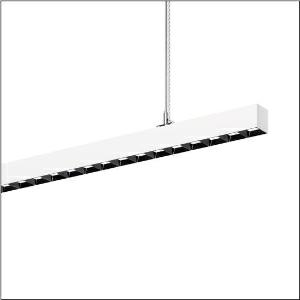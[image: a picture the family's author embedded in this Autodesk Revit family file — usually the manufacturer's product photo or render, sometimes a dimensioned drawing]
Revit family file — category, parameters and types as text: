
# Revit family: silica_r__21_51mx31tctdw_2edc
name_source: partatom
category: Lighting Fixtures
units: mm (PartAtom-declared; Revit-internal decimal feet)

## family parameters
Cut with Voids When Loaded = No
Host = Face
Light Source = No
Part Type = Normal
Room Calculation Point = No
Round Connector Dimension = Use Diameter
Shared = No

## types (1)
- --- (1 x LED, 15550 lm, 133.9 W, 6500K)
    Apparent Load = 134 VA
    CIE Flux Codes = 85 99 100 60 100
    Color Rendering = 80
    Color Temperature = 6500K
    Default Elevation = 1800 mm
    Description = Silica® 21, office luminaire, primary light control with darklight reflector, of PMMA, black, CAT 2 (L<= 3000cd/m²), light emission: direct/indirect distribution, primary light characteristic: symmetric, installation type: suspended mounting, LED, rated luminous flux: 15.550lm, luminous efficacy: 111lm/W, light colour: 8tw, colour temperature: 2700..6500K, control gear: ECG DALI, with terminal, 3+2-pole, max. 2.5mm², mains connection: 220..240V, AC, 50/60Hz, rated input power: 140.6W, luminaire housing, of aluminium, traffic white (RAL 9016), length: 3.004mm, width: 53mm, height: 53mm, protection rating (complete): IP20, insulation class (complete): insulation class I (protective earthing), certification: CE, permissible operating ambient temperature: 0..+35°C, standard: EN 50419, packaging unit: 1 piece
    Height = 53 mm
    Lamp = 1 x LED
    Lamp Light Flux = 15550 lm
    Lamp Power = 133.9 W
    Lamp count = 1
    Length = 3004 mm
    Luminous efficacy = 116 lm/W
    Manufacturer = Siteco
    ModVariant = No
    Model = 51MX31TCTDW
    Mounting Place = Ceiling
    Mounting Type = Pendant
    Number of Poles = 1
    OnlyDefault = Yes
    Power Factor = 1
    Product Name = Silica® 21
    Product group = office luminaire | ceiling pendant
    ProductGroupID = 902
    Protection Class = Protection class I
    Protection Degree = IP 20
    RLX_Detail_Level = 1
    RLX_Emergency_Light_Flux = 0 lm
    RLX_Emergency_Type = 0
    RLX_Emergency_Type_DB = No
    RlxData = <blob elided: 60833 chars, md5=bde70622>
    Socket = socket
    Standby Power = 0 W
    System Light Flux = 15550 lm
    System Power = 134 W
    Type Comments = individual setting
    Type Image = l_1335871.jpg
    URL = http://relux.com
    VarID = @adj_109699
    Voltage = 0 V
    Weight = 0.00 kg
    Width = 53 mm

## geometry (parser evidence)
native form markers: Blend x4, Sweep x14
no freeform markers — native parametric forms only
